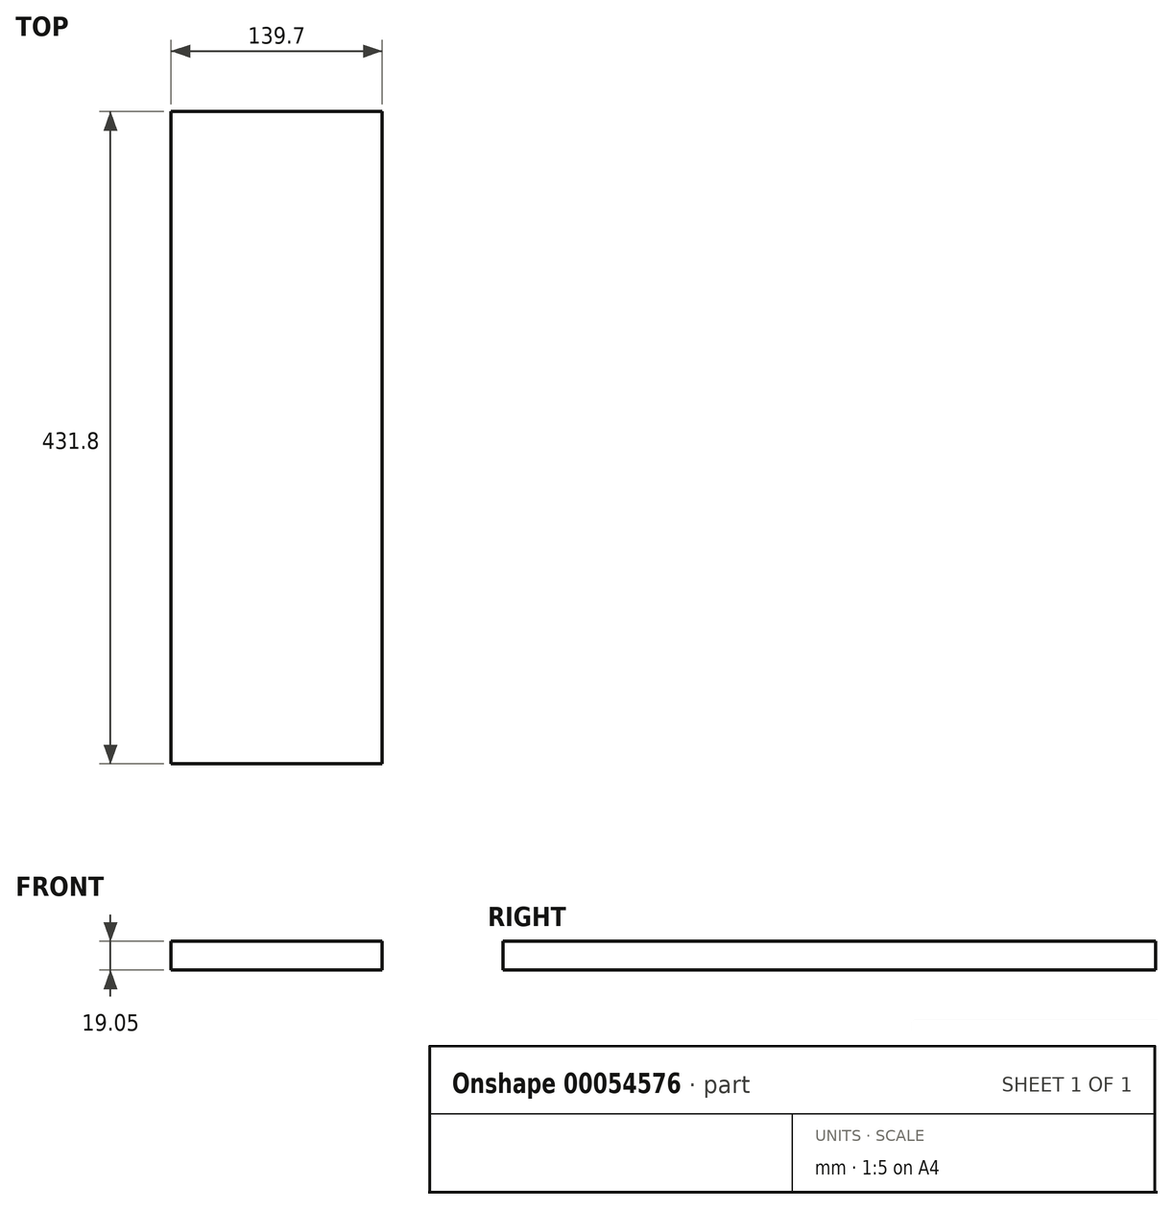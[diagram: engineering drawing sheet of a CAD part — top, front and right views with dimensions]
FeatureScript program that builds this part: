
annotation { "Feature Type Name" : "Feature", "Feature Type Description" : "" }
export const myFeature = defineFeature(function(context is Context, id is Id, definition is map)
    precondition{}
    {
        {
            var Q0;
            Q0=qCreatedBy(makeId("Front.planeOp"),FACE);
            var sketch = newSketch(context, id + "F0", { "sketchPlane" : qUnion([Q0])});
            skLineSegment(sketch, "E0.bottom", {"start": v(0, 0) * mm, "end": v(139.7, 0) * mm});
            skLineSegment(sketch, "E0.top", {"start": v(0, 19.05) * mm, "end": v(139.7, 19.05) * mm});
            skLineSegment(sketch, "E0.left", {"start": v(0, 0) * mm, "end": v(0, 19.05) * mm});
            skLineSegment(sketch, "E0.right", {"start": v(139.7, 0) * mm, "end": v(139.7, 19.05) * mm});
            skSolve(sketch);
        }
        {
            var Q0;
            Q0 = qSketchRegion(id + "F0", true);
            extrude(context, id + "F1", {"entities" : qUnion([Q0]), "depth" : 431.8 * mm});
        }
    });
